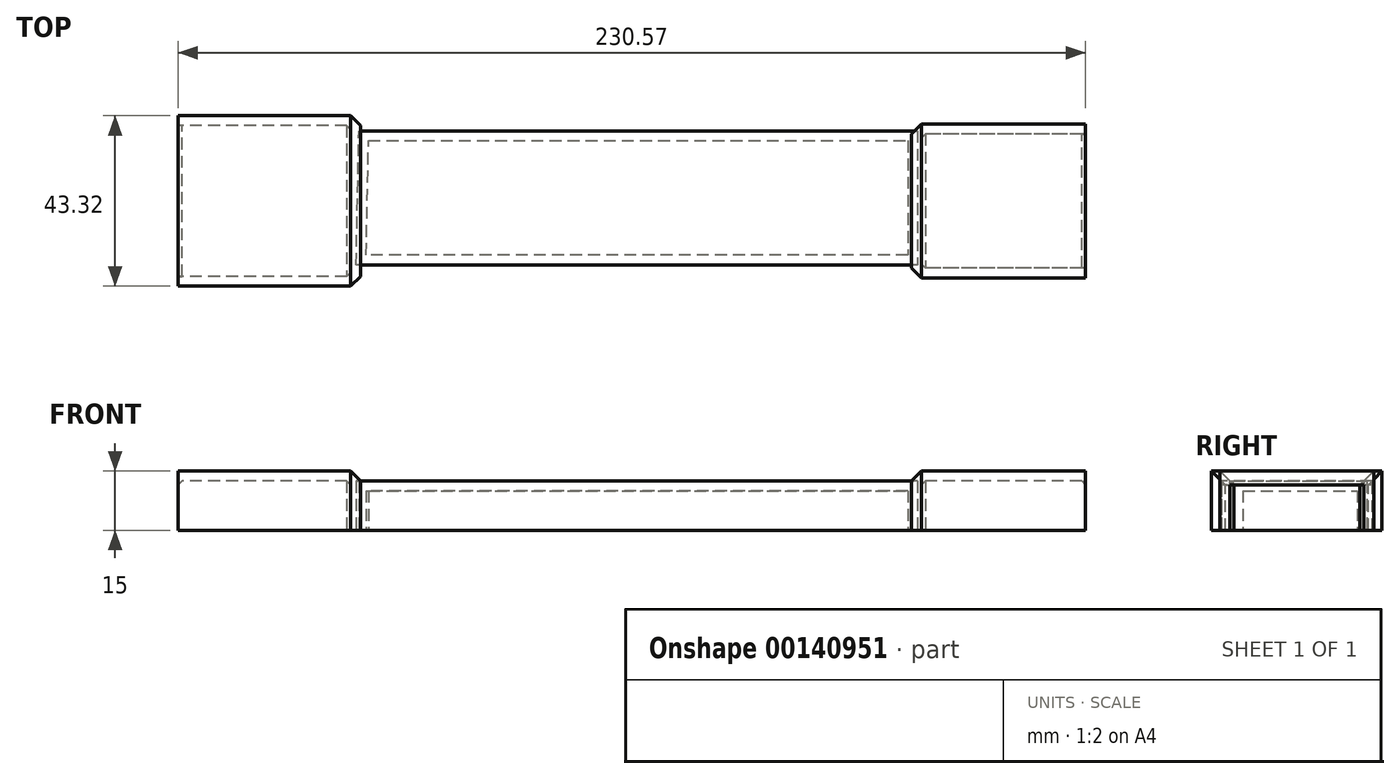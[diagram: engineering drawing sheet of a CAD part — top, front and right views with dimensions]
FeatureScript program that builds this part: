
annotation { "Feature Type Name" : "Feature", "Feature Type Description" : "" }
export const myFeature = defineFeature(function(context is Context, id is Id, definition is map)
    precondition{}
    {
        {
            var Q0;
            Q0=qCreatedBy(makeId("Top.planeOp"),FACE);
            var sketch = newSketch(context, id + "F0", { "sketchPlane" : qUnion([Q0])});
            skLineSegment(sketch, "E0.bottom", {"start": v(128.25, 19.55) * mm, "end": v(83.99, 19.55) * mm});
            skLineSegment(sketch, "E0.top", {"start": v(128.25, -19.55) * mm, "end": v(83.99, -19.55) * mm});
            skLineSegment(sketch, "E0.left", {"start": v(128.25, 19.55) * mm, "end": v(128.25, -19.55) * mm});
            skLineSegment(sketch, "E0.right", {"start": v(83.99, 19.55) * mm, "end": v(83.99, -19.55) * mm});
            skPoint(sketch, "E0.middle", {"position": v(106.12, 0) * mm});
            skSolve(sketch);
        }
        {
            var Q0;
            Q0=qCreatedBy(makeId("Top.planeOp"),FACE);
            var sketch = newSketch(context, id + "F9", { "sketchPlane" : qUnion([Q0])});
            skLineSegment(sketch, "E1.bottom", {"start": v(-55.97, 21.66) * mm, "end": v(-102.32, 21.66) * mm});
            skLineSegment(sketch, "E1.top", {"start": v(-55.97, -21.66) * mm, "end": v(-102.32, -21.66) * mm});
            skLineSegment(sketch, "E1.left", {"start": v(-55.97, 21.66) * mm, "end": v(-55.97, -21.66) * mm});
            skLineSegment(sketch, "E1.right", {"start": v(-102.32, 21.66) * mm, "end": v(-102.32, -21.66) * mm});
            skPoint(sketch, "E1.middle", {"position": v(-79.14, 0) * mm});
            skSolve(sketch);
        }
        {
            var Q0;
            Q0=makeQuery(id+"F9.imprint","IMPRINT",FACE,{"disambiguationData":[TD([[makeQuery(id+"F9.imprint","IMPRINT",EDGE,{"derivedFrom":sQuery(id+"F9.wireOp",EDGE,"E1.bottom")}),1.0]])]});
            var Q1;
            Q1=makeQuery(id+"F0.imprint","IMPRINT",FACE,{"disambiguationData":[TD([[makeQuery(id+"F0.imprint","IMPRINT",EDGE,{"derivedFrom":sQuery(id+"F0.wireOp",EDGE,"E0.bottom")}),1.0]])]});
            extrude(context, id + "F10", {"entities" : qUnion([Q0, Q1]), "depth" : 15 * mm});
        }
        {
            var Q0;
            Q0=makeQuery(id+"F10.opExtrude","SWEPT_EDGE",EDGE,{"disambiguationData":[OSD([sQuery(id+"F0.wireOp",EDGE,"E0.bottom"),sQuery(id+"F0.wireOp",EDGE,"E0.right")])]});
            var Q1;
            Q1=makeQuery(id+"F10.opExtrude","SWEPT_EDGE",EDGE,{"disambiguationData":[OSD([sQuery(id+"F0.wireOp",EDGE,"E0.top"),sQuery(id+"F0.wireOp",EDGE,"E0.right")])]});
            var Q2;
            Q2=makeQuery(id+"F10.opExtrude","CAP_EDGE",EDGE,{"disambiguationData":[OSD([sQuery(id+"F0.wireOp",EDGE,"E0.right")])],"isStart":false});
            chamfer(context, id + "F1", {"entities" : qUnion([Q0, Q1, Q2]), "width" : 2.5 * mm, "tangentPropagation" : true});
        }
        {
            var Q0;
            Q0=makeQuery(id+"F10.opExtrude","SWEPT_EDGE",EDGE,{"disambiguationData":[OSD([sQuery(id+"F9.wireOp",EDGE,"E1.top"),sQuery(id+"F9.wireOp",EDGE,"E1.left")])]});
            var Q1;
            Q1=makeQuery(id+"F10.opExtrude","CAP_EDGE",EDGE,{"disambiguationData":[OSD([sQuery(id+"F9.wireOp",EDGE,"E1.left")])],"isStart":false});
            var Q2;
            Q2=makeQuery(id+"F10.opExtrude","SWEPT_EDGE",EDGE,{"disambiguationData":[OSD([sQuery(id+"F9.wireOp",EDGE,"E1.bottom"),sQuery(id+"F9.wireOp",EDGE,"E1.left")])]});
            chamfer(context, id + "F2", {"entities" : qUnion([Q0, Q1, Q2]), "width" : 2.5 * mm, "tangentPropagation" : true});
        }
        {
            var Q0;
            Q0=qCreatedBy(makeId("Top.planeOp"),FACE);
            var sketch = newSketch(context, id + "F11", { "sketchPlane" : qUnion([Q0])});
            skLineSegment(sketch, "E2", {"start": v(-56.4, 17.82) * mm, "end": v(85.58, 17.82) * mm});
            skLineSegment(sketch, "E3", {"start": v(85.58, 17.82) * mm, "end": v(85.58, -16.22) * mm});
            skLineSegment(sketch, "E4", {"start": v(85.58, -16.22) * mm, "end": v(-57.07, -16.22) * mm});
            skLineSegment(sketch, "E5", {"start": v(-57.07, -16.22) * mm, "end": v(-56.4, 17.82) * mm});
            skSolve(sketch);
        }
        {
            var Q0;
            Q0=makeQuery(id+"F11.imprint","IMPRINT",FACE,{"disambiguationData":[TD([[makeQuery(id+"F11.imprint","IMPRINT",EDGE,{"derivedFrom":sQuery(id+"F11.wireOp",EDGE,"E2")}),-1.0]])]});
            extrude(context, id + "F3", {"entities" : qUnion([Q0]), "depth" : 12.5 * mm});
        }
        {
            var Q0;
            Q0=makeQuery(id+"F3.opExtrude","CAP_FACE",FACE,{"disambiguationData":[OSD([sQuery(id+"F11.wireOp",EDGE,"E2"),sQuery(id+"F11.wireOp",EDGE,"E3"),sQuery(id+"F11.wireOp",EDGE,"E4"),sQuery(id+"F11.wireOp",EDGE,"E5")])],"isStart":true});
            var Q1;
            Q1=makeQuery(id+"F10.opExtrude","CAP_FACE",FACE,{"disambiguationData":[OSD([sQuery(id+"F9.wireOp",EDGE,"E1.bottom"),sQuery(id+"F9.wireOp",EDGE,"E1.top"),sQuery(id+"F9.wireOp",EDGE,"E1.left"),sQuery(id+"F9.wireOp",EDGE,"E1.right")])],"isStart":true});
            var Q2;
            Q2=makeQuery(id+"F10.opExtrude","CAP_FACE",FACE,{"disambiguationData":[OSD([sQuery(id+"F0.wireOp",EDGE,"E0.bottom"),sQuery(id+"F0.wireOp",EDGE,"E0.top"),sQuery(id+"F0.wireOp",EDGE,"E0.left"),sQuery(id+"F0.wireOp",EDGE,"E0.right")])],"isStart":true});
            shell(context, id + "F4", {"entities" : qUnion([Q0, Q1, Q2]), "thickness" : 2.5 * mm});
        }
        {
            var Q0;
            Q0=makeQuery(id+"F3.opExtrude","CAP_FACE",FACE,{"disambiguationData":[OSD([sQuery(id+"F11.wireOp",EDGE,"E2"),sQuery(id+"F11.wireOp",EDGE,"E3"),sQuery(id+"F11.wireOp",EDGE,"E4"),sQuery(id+"F11.wireOp",EDGE,"E5")])],"isStart":false});
            var sketch = newSketch(context, id + "F12", { "sketchPlane" : qUnion([Q0])});
            skLineSegment(sketch, "E6", {"start": v(-42.8, 0.8) * mm, "end": v(68.5, 0.8) * mm});
            skPoint(sketch, "E6.startSnap0", {"position": v(-56.74, 0.8) * mm});
            skSolve(sketch);
        }
        {
            var Q0;
            Q0=makeQuery(id+"F12.imprint","IMPRINT",FACE,{"disambiguationData":[TD([[makeQuery(id+"F12.imprint","IMPRINT",EDGE,{"derivedFrom":makeQuery(id+"F3.opExtrude","CAP_EDGE",EDGE,{"disambiguationData":[OSD([sQuery(id+"F11.wireOp",EDGE,"E2")])],"isStart":false})}),-1.0]])]});
            var sketch = newSketch(context, id + "F5", { "sketchPlane" : qUnion([Q0])});
            skLineSegment(sketch, "E7", {"start": v(-41.04, -8.17) * mm, "end": v(69.8, -8.17) * mm});
            skSolve(sketch);
        }
        {
            var Q0;
            Q0=makeQuery(id+"F5.imprint","IMPRINT",FACE,{"disambiguationData":[TD([[makeQuery(id+"F5.imprint","IMPRINT",EDGE,{"derivedFrom":makeQuery(id+"F12.imprint","IMPRINT",EDGE,{"derivedFrom":makeQuery(id+"F3.opExtrude","CAP_EDGE",EDGE,{"disambiguationData":[OSD([sQuery(id+"F11.wireOp",EDGE,"E2")])],"isStart":false})})}),-1.0]])]});
            var sketch = newSketch(context, id + "F6", { "sketchPlane" : qUnion([Q0])});
            skLineSegment(sketch, "E8", {"start": v(-41.5, 7.73) * mm, "end": v(68.95, 7.73) * mm});
            skSolve(sketch);
        }
        {
            var Q0;
            Q0=sQuery(id+"F6.wireOp",EDGE,"E8");
            var Q1;
            Q1=sQuery(id+"F12.wireOp",EDGE,"E6");
            var Q2;
            Q2=sQuery(id+"F5.wireOp",EDGE,"E7");
            loft(context, id + "F7", {"bodyType" : ToolBodyType.SURFACE, "wireProfilesArray" : [{ "wireProfileEntities" : qUnion([Q0]) }, { "wireProfileEntities" : qUnion([Q1]) }, { "wireProfileEntities" : qUnion([Q2]) }]});
        }
        {
            var Q0;
            {var subQ0=sQuery(id+"F0.wireOp",EDGE,"E0.left");Q0=makeQuery(id+"F4.opShell","OFFSET_EDGE",EDGE,{"disambiguationData":[OSD([subQ0]),TDD([makeQuery(id+"F10.opExtrude","CAP_EDGE",EDGE,{"disambiguationData":[OSD([subQ0])],"isStart":true})])]});}
            chamfer(context, id + "F8", {"entities" : qUnion([Q0]), "width" : 14 * mm, "tangentPropagation" : true});
        }
        {
            var Q0;
            {var subQ0=sQuery(id+"F9.wireOp",EDGE,"E1.right");Q0=makeQuery(id+"F4.opShell","OFFSET_EDGE",EDGE,{"disambiguationData":[OSD([subQ0]),TDD([makeQuery(id+"F10.opExtrude","CAP_EDGE",EDGE,{"disambiguationData":[OSD([subQ0])],"isStart":true})])]});}
            chamfer(context, id + "F13", {"entities" : qUnion([Q0]), "width" : 14 * mm, "tangentPropagation" : true});
        }
    });
